# Revit family: IS_LDV_E2671_BIM_GB
name_source: partatom
category: Plumbing Fixtures
units: mm (PartAtom-declared; Revit-internal decimal feet)

## family parameters
Cut with Voids When Loaded = No
Host = Face
Maintain Annotation Orientation = No
OmniClass Number = 23.45.05.14.14.14
OmniClass Title = Clinic Sinks
Part Type = Normal
Room Calculation Point = No
Round Connector Dimension = Use Diameter
Shared = Yes

## types (1)
- E267101 - LDV SEMI PEDESTAL WHITE BXD
    Accessories = https://www.idealstandard.co.uk
    AreaUnits = millimeters
    Assembly Code = C1030200
    AssetType = Fixed
    BIMObjectName = IS_LDV_Semiped_E2671
    BarCode = 5017830562559
    Brand = Ideal Standard
    CWFU = 0
    Color = White
    ConnectionType = Plumbing
    Cost = 0 $
    Default Elevation = 0 mm  [stored 0 ft]
    Description = La Dolce Vita® semi-pedestal for La Dolce Vita® vanity basins, including fixation TV63667, white
    DrainSize = 46 mm  [stored 0.150919 ft]
    DurationUnit = year
    ECA = No
    EPD = https://www.idealstandard.co.uk
    ExpectedLife = 25
    Features = La Dolce Vita® semi-pedestal for La Dolce Vita® vanity basins, including fixation TV63667, white, boxed
    Finish = white
    HWFU = 0
    Help = https://www.idealstandard.co.uk
    IfcExportAs = IfcSanitaryType
    IfcExportType = PEDESTAL
    InstallationInstructions = https://www.idealstandard.co.uk
    LinearUnits = millimeters
    Manufacturer = Ideal Standard
    ManufacturerURL = https://www.idealstandard.co.uk
    Material = Fine Fireclay
    Model = E267101
    ModelNumber = E267101
    ModelReference = La Dolce Vita® semi-pedestal for La Dolce Vita® vanity basins, including fixation TV63667, white
    NBSDescription = Pedestal washbasins
    NBSReference = Pr_40_20_96_63
    Name = Semiped_LDV_E2671_IdealStandard
    NettWeight = 6,3
    NominalHeight = 340 mm
    NominalLength = 279 mm
    NominalWidth = 177 mm
    ProductInformation = https://www.idealstandard.co.uk
    Shape = Sculptured
    Size = 180x280x340mm
    Space = Internal
    URL = https://www.idealstandard.co.uk
    Uniclass2015Description = Pedestal washbasins
    Uniclass2015Version = Products v1.33
    Version = 1
    VolumeUnits = Litres
    WFU = 0
    WRAS = No
    WarrantyDescription = Manufacturers Warranty
    WarrantyDurationParts = 99
    WarrantyDurationUnit = year
    WarrantyGuarantorParts = Ideal Standard
    WaterEfficientProduct = No

note: [stored X ft] marks values corroborated as IEEE doubles in the binary element streams (Revit-internal decimal feet)

## geometry (parser evidence)
native form markers: Sweep x1
no freeform markers — native parametric forms only
